# Revit family: LOROWERK 01393-100X
name_source: partatom
category: Sanitärinstallationen
revit_build: Autodesk Revit 2017 (Build: 20160225_1515(x64)
units: mm (PartAtom-declared; Revit-internal decimal feet)

## family parameters
Arbeitsebenenbasiert = Nein
Beim Laden mit Abzugskörper schneiden = Nein
Bemaßung runder Anschluss = Durchmesser verwenden
Gemeinsam genutzt = Nein
Immer vertikal = Ja
Raumberechnungspunkt = Nein
Teiletyp = Normal

## types (1)
- LOROWERK 01393-100X
    38.710.01.13 = seitlich
    38.710.01.5 = DN
    Abdichtvarianten = mit Klemmflansch
    Abflussstutzen Ausführung = waagerecht
    Ablaufanschluss = 1
    Art der Nenn-/Betriebsspannung = nicht zutreffend
    BIM = https://media.stage.bim.site
    Beschreibung = LORO-RAINSTAR Attikaabläufe, Serie 88, Attika-Distant, ohne Aufkantung
    Bestellmenge (Multiplikator) = 1
    CONNECTOR0_DIAMETER_dZ_0r = 100 mm  [stored 0.328084 ft]
    CONNECTOR0_dZ_00 = 67 mm
    CONNECTOR0_dZ_01 = 67 mm
    CONNECTOR0_ref_dZ = 67 mm
    CONNECTOR1_DIAMETER_dNBN0_0r = 100 mm  [stored 0.328084 ft]
    CONNECTOR1_dNBN0_00 = 216 mm
    CONNECTOR1_dNBN0_01 = 290 mm
    CONNECTOR1_ref_dNBN0 = 216 mm
    CONNECTOR1_ref_dNBN1 = 49 mm
    DATANORM = 01393.100X
    Einbaubreite [m] = 0.24
    Einbautiefe [m] = 0.055
    Feuerwiderstandsklasse = keine Feuerwiderstandsklasse
    Feuerwiderstandsklasse nachrüstbar = nein
    GTIN = 4038088074169
    Gehäuseanschlussarten = Ablauf punktförmig
    Geruchsverschluss = ohne Geruchsverschluss
    HAN = 01393.100X
    Heizung = ohne Heizung
    Hersteller = LOROWERK K.H. Vahlbrauk GmbH & Co. KG
    Ist System = Nein
    Ist Zubehör = Nein
    Kommentar = Serie 88, Attika-Distant, ohne Aufkantung
    Nenndruck = 422
    Nenndrucksystem = 270
    Nennweitensystem = PN
    Potenzialausgleich (Erdungsanschluss)   vorhanden = ja
    Produktbezeichnung = LORO-RAINSTAR 88 Attikanotablauf, ohne Aufkant., Edelst., Klemmfl., Druckström., DN100
    Produktklassifikation = Attikaablauf
    Produktname = LORO-RAINSTAR 88 Attikanotablauf, ohne Aufkant., Edelst., Klemmfl., Druckström., DN100
    Produktvideo = https://media.stage.bim.site
    Sperrwasserhöhe [m] = 0
    Typname = LORO-RAINSTAR 88 Attikanotablauf, ohne Aufkant., Edelst., Klemmfl., Druckström., DN100
    VDIBSN = 0020090000020020000010020010010000000030020000001400000001
    Werkstoff des Ablaufkörpers = nicht rostender Stahl
    Wärmedämmung = ohne Wärmedämmung
    elektrischer Anschluss = nein

note: [stored X ft] marks values corroborated as IEEE doubles in the binary element streams (Revit-internal decimal feet)
